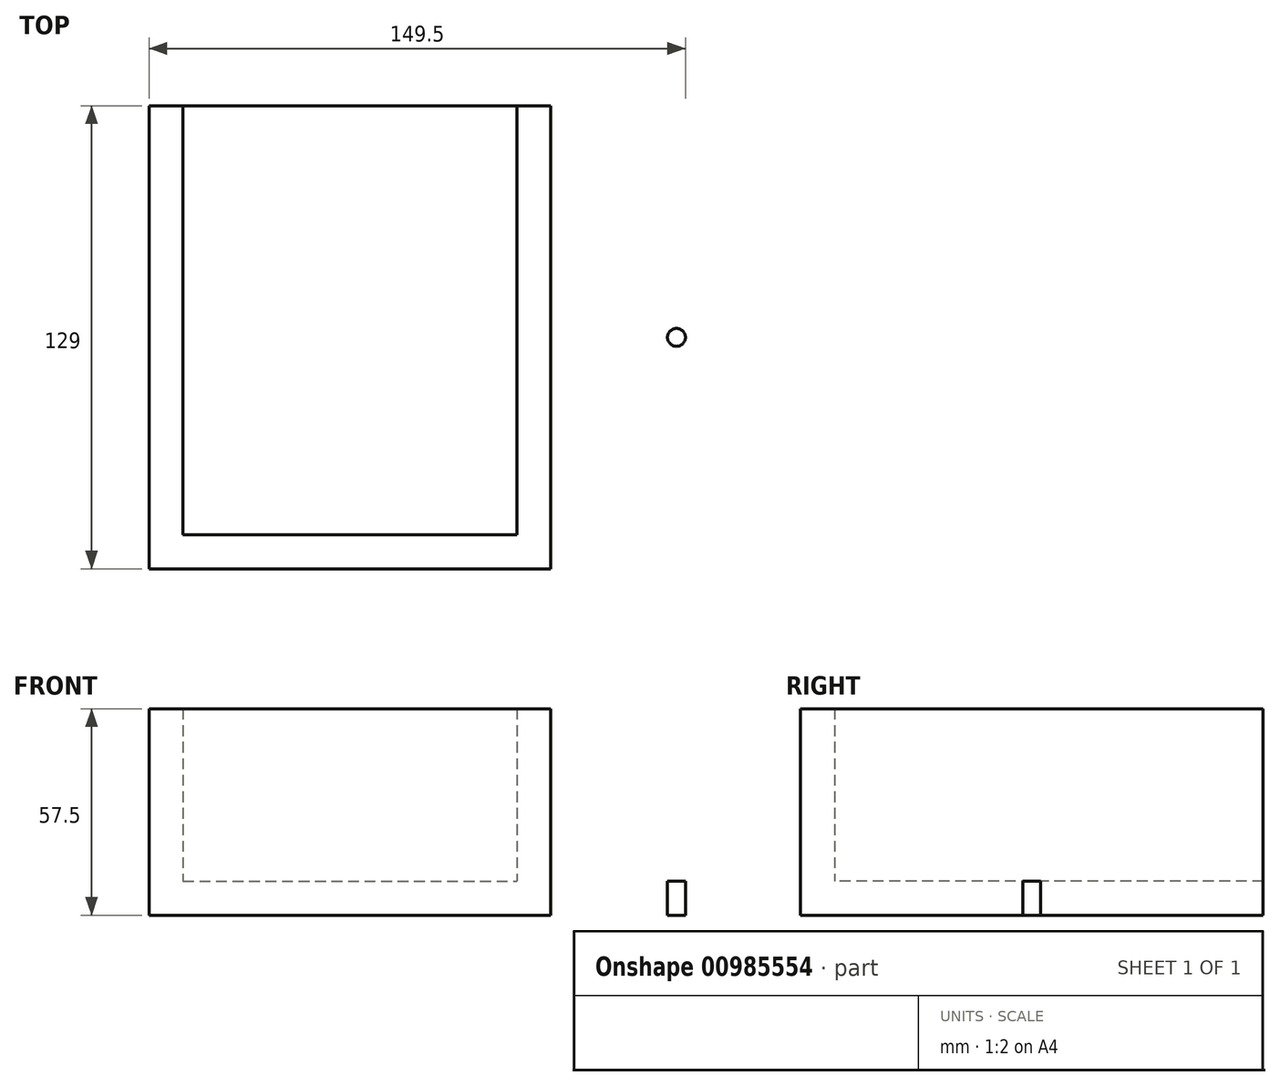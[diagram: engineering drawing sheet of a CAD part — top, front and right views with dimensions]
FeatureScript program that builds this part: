
annotation { "Feature Type Name" : "Feature", "Feature Type Description" : "" }
export const myFeature = defineFeature(function(context is Context, id is Id, definition is map)
    precondition{}
    {
        {
            var Q0;
            Q0=qCreatedBy(makeId("Top.planeOp"),FACE);
            var sketch = newSketch(context, id + "F0", { "sketchPlane" : qUnion([Q0])});
            skLineSegment(sketch, "E0", {"start": v(0, 0) * mm, "end": v(0, 129) * mm});
            skLineSegment(sketch, "E1", {"start": v(0, 129) * mm, "end": v(302.5, 129) * mm});
            skLineSegment(sketch, "E2", {"start": v(302.5, 129) * mm, "end": v(302.5, 83.1) * mm});
            skLineSegment(sketch, "E3", {"start": v(302.5, 83.1) * mm, "end": v(310, 83.1) * mm});
            skLineSegment(sketch, "E4", {"start": v(310, 83.1) * mm, "end": v(310, 33.5) * mm});
            skLineSegment(sketch, "E5", {"start": v(310, 33.5) * mm, "end": v(426, 33.5) * mm});
            skLineSegment(sketch, "E6", {"start": v(426, 33.5) * mm, "end": v(426, 114.04) * mm});
            skLineSegment(sketch, "E7", {"start": v(426, 114.04) * mm, "end": v(438, 114.04) * mm});
            skLineSegment(sketch, "E8", {"start": v(438, 114.04) * mm, "end": v(438, 43) * mm});
            skLineSegment(sketch, "E9", {"start": v(438, 43) * mm, "end": v(556, 43) * mm});
            skLineSegment(sketch, "E10", {"start": v(556, 43) * mm, "end": v(556, 0) * mm});
            skLineSegment(sketch, "E11", {"start": v(556, 0) * mm, "end": v(0, 0) * mm});
            skSolve(sketch);
        }
        {
            var Q0;
            Q0 = qSketchRegion(id + "F0", true);
            extrude(context, id + "F1", {"entities" : qUnion([Q0]), "depth" : 9.5 * mm, "offsetDistance" : 25.4 * mm});
        }
        {
            var Q0;
            Q0=makeQuery(id+"F1.opExtrude","CAP_FACE",FACE,{"disambiguationData":[OSD([sQuery(id+"F0.wireOp",EDGE,"E0"),sQuery(id+"F0.wireOp",EDGE,"E1"),sQuery(id+"F0.wireOp",EDGE,"E2"),sQuery(id+"F0.wireOp",EDGE,"E3"),sQuery(id+"F0.wireOp",EDGE,"E4"),sQuery(id+"F0.wireOp",EDGE,"E5"),sQuery(id+"F0.wireOp",EDGE,"E6"),sQuery(id+"F0.wireOp",EDGE,"E7"),sQuery(id+"F0.wireOp",EDGE,"E8"),sQuery(id+"F0.wireOp",EDGE,"E9"),sQuery(id+"F0.wireOp",EDGE,"E10"),sQuery(id+"F0.wireOp",EDGE,"E11")])],"isStart":false});
            var sketch = newSketch(context, id + "F2", { "sketchPlane" : qUnion([Q0])});
            skLineSegment(sketch, "E12.bottom", {"start": v(0, 129) * mm, "end": v(9.5, 129) * mm});
            skLineSegment(sketch, "E12.top", {"start": v(0, 0) * mm, "end": v(9.5, 0) * mm});
            skLineSegment(sketch, "E12.left", {"start": v(0, 129) * mm, "end": v(0, 0) * mm});
            skLineSegment(sketch, "E12.right", {"start": v(9.5, 129) * mm, "end": v(9.5, 0) * mm});
            skLineSegment(sketch, "E13.bottom", {"start": v(0, 0) * mm, "end": v(112, 0) * mm});
            skLineSegment(sketch, "E13.top", {"start": v(0, 9.5) * mm, "end": v(112, 9.5) * mm});
            skLineSegment(sketch, "E13.left", {"start": v(0, 0) * mm, "end": v(0, 9.5) * mm});
            skLineSegment(sketch, "E13.right", {"start": v(112, 0) * mm, "end": v(112, 9.5) * mm});
            skLineSegment(sketch, "E14.bottom", {"start": v(112, 0) * mm, "end": v(102.5, 0) * mm});
            skLineSegment(sketch, "E14.top", {"start": v(112, 129) * mm, "end": v(102.5, 129) * mm});
            skLineSegment(sketch, "E14.left", {"start": v(112, 0) * mm, "end": v(112, 129) * mm});
            skLineSegment(sketch, "E14.right", {"start": v(102.5, 0) * mm, "end": v(102.5, 129) * mm});
            skSolve(sketch);
        }
        {
            var Q0;
            Q0 = qSketchRegion(id + "F2", true);
            extrude(context, id + "F3", {"entities" : qUnion([Q0]), "operationType" : NewBodyOperationType.ADD, "depth" : 48 * mm, "offsetDistance" : 25.4 * mm});
        }
        {
            var Q0;
            {var subQ0=sQuery(id+"F0.wireOp",EDGE,"E10");var subQ1=sQuery(id+"F0.wireOp",EDGE,"E9");var subQ2=sQuery(id+"F0.wireOp",EDGE,"E8");var subQ3=sQuery(id+"F0.wireOp",EDGE,"E7");var subQ4=sQuery(id+"F0.wireOp",EDGE,"E6");var subQ5=sQuery(id+"F0.wireOp",EDGE,"E5");var subQ6=sQuery(id+"F0.wireOp",EDGE,"E1");var subQ7=sQuery(id+"F0.wireOp",EDGE,"E2");var subQ8=sQuery(id+"F0.wireOp",EDGE,"E3");var subQ9=sQuery(id+"F0.wireOp",EDGE,"E4");var subQ10=sQuery(id+"F0.wireOp",EDGE,"E11");Q0=makeQuery(id+"F3.boolean.opBoolean","SPLIT",FACE,{"disambiguationData":[TD([makeQuery(id+"F1.opExtrude","SWEPT_FACE",FACE,{"disambiguationData":[OSD([subQ7])]})])],"derivedFrom":makeQuery(id+"F1.opExtrude","CAP_FACE",FACE,{"disambiguationData":[OSD([sQuery(id+"F0.wireOp",EDGE,"E0"),subQ6,subQ7,subQ8,subQ9,subQ5,subQ4,subQ3,subQ2,subQ1,subQ0,subQ10])],"isStart":false})});}
            var sketch = newSketch(context, id + "F4", { "sketchPlane" : qUnion([Q0])});
            skLineSegment(sketch, "E15", {"start": v(112, 64.5) * mm, "end": v(320.03, 64.5) * mm});
            skCircle(sketch, "E16", {"center": v(147, 64.5) * mm, "radius": 2.5 * mm});
            skCircle(sketch, "E17", {"center": v(281, 64.5) * mm, "radius": 2.5 * mm});
            skSolve(sketch);
        }
        {
            var Q0;
            {var subQ0=sQuery(id+"F4.wireOp",EDGE,"E16");var subQ1=sQuery(id+"F4.wireOp",EDGE,"E15");var subQ2=makeQuery(id+"F4.imprint","INTERSECT",VERTEX,{"disambiguationData":[OD(0.0)],"derivedFrom":[subQ1,subQ0]});Q0=makeQuery(id+"F4.imprint","IMPRINT",FACE,{"disambiguationData":[TD([[makeQuery(id+"F4.imprint","IMPRINT",EDGE,{"disambiguationData":[TD([[subQ2,-1.0]])],"derivedFrom":subQ1}),1.0]])]});}
            var Q1;
            {var subQ0=sQuery(id+"F4.wireOp",EDGE,"E16");var subQ1=sQuery(id+"F4.wireOp",EDGE,"E15");var subQ2=makeQuery(id+"F4.imprint","INTERSECT",VERTEX,{"disambiguationData":[OD(0.0)],"derivedFrom":[subQ1,subQ0]});Q1=makeQuery(id+"F4.imprint","IMPRINT",FACE,{"disambiguationData":[TD([[makeQuery(id+"F4.imprint","IMPRINT",EDGE,{"disambiguationData":[TD([[subQ2,-1.0]])],"derivedFrom":subQ1}),-1.0]])]});}
            var Q2;
            {var subQ0=sQuery(id+"F4.wireOp",EDGE,"E17");var subQ1=sQuery(id+"F4.wireOp",EDGE,"E15");var subQ2=makeQuery(id+"F4.imprint","INTERSECT",VERTEX,{"disambiguationData":[OD(0.0)],"derivedFrom":[subQ1,subQ0]});Q2=makeQuery(id+"F4.imprint","IMPRINT",FACE,{"disambiguationData":[TD([[makeQuery(id+"F4.imprint","IMPRINT",EDGE,{"disambiguationData":[TD([[subQ2,-1.0]])],"derivedFrom":subQ1}),-1.0]])]});}
            var Q3;
            {var subQ0=sQuery(id+"F4.wireOp",EDGE,"E17");var subQ1=sQuery(id+"F4.wireOp",EDGE,"E15");var subQ2=makeQuery(id+"F4.imprint","INTERSECT",VERTEX,{"disambiguationData":[OD(0.0)],"derivedFrom":[subQ1,subQ0]});Q3=makeQuery(id+"F4.imprint","IMPRINT",FACE,{"disambiguationData":[TD([[makeQuery(id+"F4.imprint","IMPRINT",EDGE,{"disambiguationData":[TD([[subQ2,-1.0]])],"derivedFrom":subQ1}),1.0]])]});}
            var Q4;
            Q4=sQuery(id+"F4.wireOp",EDGE,"E16");
            var Q5;
            Q5=sQuery(id+"F4.wireOp",EDGE,"E17");
            extrude(context, id + "F5", {"entities" : qUnion([Q0, Q1, Q2, Q3]), "operationType" : NewBodyOperationType.REMOVE, "surfaceEntities" : qUnion([Q4, Q5]), "oppositeDirection" : true, "depth" : 25.4 * mm, "offsetDistance" : 25.4 * mm});
        }
    });
